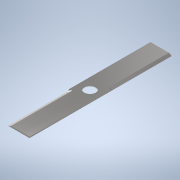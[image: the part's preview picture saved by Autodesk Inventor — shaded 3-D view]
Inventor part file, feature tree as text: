
AUTODESK INVENTOR PART (.ipt)
format: ipt  version: 2022 (Build 260153000, 153)  size: 138,240 bytes
history: native  units: in
note: dims shown in document units (in); Inventor stores cm internally (conversion verified against a paired STEP export)
features: extrude x2, sketch x2, fillet x1, pattern_circular x1
ambient origin geometry x8: Origin, YZ Plane, XZ Plane, XY Plane, X Axis, Y Axis, Z Axis, Center Point
bodies: Solid1 (feature_tree)
feature tree (6):
  extrude  "Extrusion1"  Depth=1.1811in
  extrude  "Extrusion2"  Depth=0.075in TaperAngle=0.0deg
  fillet  "Fillet1"  Radius=0.1718in
  pattern_circular  "Circular Pattern1"  [2 undecoded]
  sketch  "Sketch1"  dims[d0=0.6299in d1=1.1811in]
  sketch  "Sketch2"  dims[d2=7.875in d3=0.075in d4=0.0in d6=0.1718in d7=3.375in d8=0.0in d9=0.125in d10=0.7874in d11=360.0deg]
note: 2 required parameter values undecoded (feature->parameter linkage not recoverable at this tier; creation-order binding heuristic only, values carry confidence <= 0.55)
